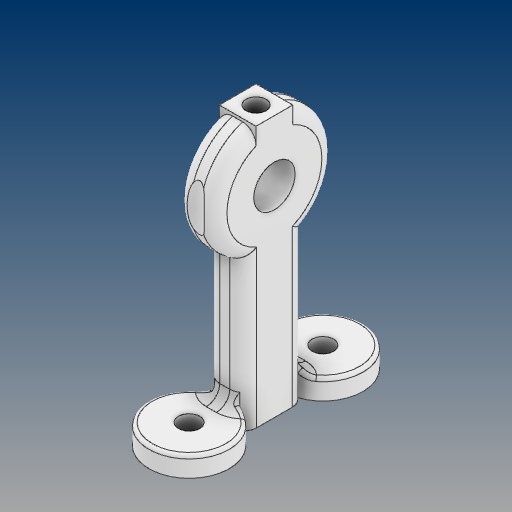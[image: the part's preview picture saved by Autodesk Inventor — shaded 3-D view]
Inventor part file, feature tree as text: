
AUTODESK INVENTOR PART (.ipt)
format: ipt  version: 2021 (Build 250183000, 183)  size: 347,136 bytes
history: native  units: mm
features: sketch x5, extrude x4, fillet x3, projected_geometry x2, hole x1, plane x1
ambient origin geometry x8: Origin, YZ Plane, XZ Plane, XY Plane, X Axis, Y Axis, Z Axis, Center Point
bodies: Solid1 (feature_tree)
feature tree (16):
  extrude  "Extrusion1"  Depth=12.0mm
  extrude  "Extrusion2"  Depth=3.0mm TaperAngle=0.0deg
  hole  "Hole1"  [1 undecoded]
  fillet  "Fillet1"  Radius=6.0mm
  plane  "Work Plane1"
  extrude  "Extrusion3"  Depth=2.0mm
  extrude  "Extrusion4"  Depth=5.5mm
  fillet  "Fillet2"  Radius=2.0mm
  fillet  "Fillet3"  Radius=3.0mm
  sketch  "Sketch1"  dims[d0=20.0mm d1=12.0mm]
  sketch  "Sketch2"  dims[d2=5.5mm d3=3.0mm d4=0.0mm]
  projected_geometry  "Projected Loop1"
  sketch  "Sketch3"  dims[d5=6.2mm d6=30.0mm d7=6.0mm]
  projected_geometry  "Projected Loop2"
  sketch  "Sketch4"  dims[d9=5.5mm d10=0.0mm]
  sketch  "Sketch5"  dims[d11=3.2mm d12=6.0mm d13=4.0mm d14=2.0mm d15=90.0deg d16=8.0mm d17=20.594885mm d18=2.0mm d19=5.5mm d21=2.0mm d22=0.0mm d23=3.0mm d24=7.75mm d25=0.0mm d26=2.0mm d27=0.5mm]
note: 1 required parameter value undecoded (feature->parameter linkage not recoverable at this tier; creation-order binding heuristic only, values carry confidence <= 0.55)
